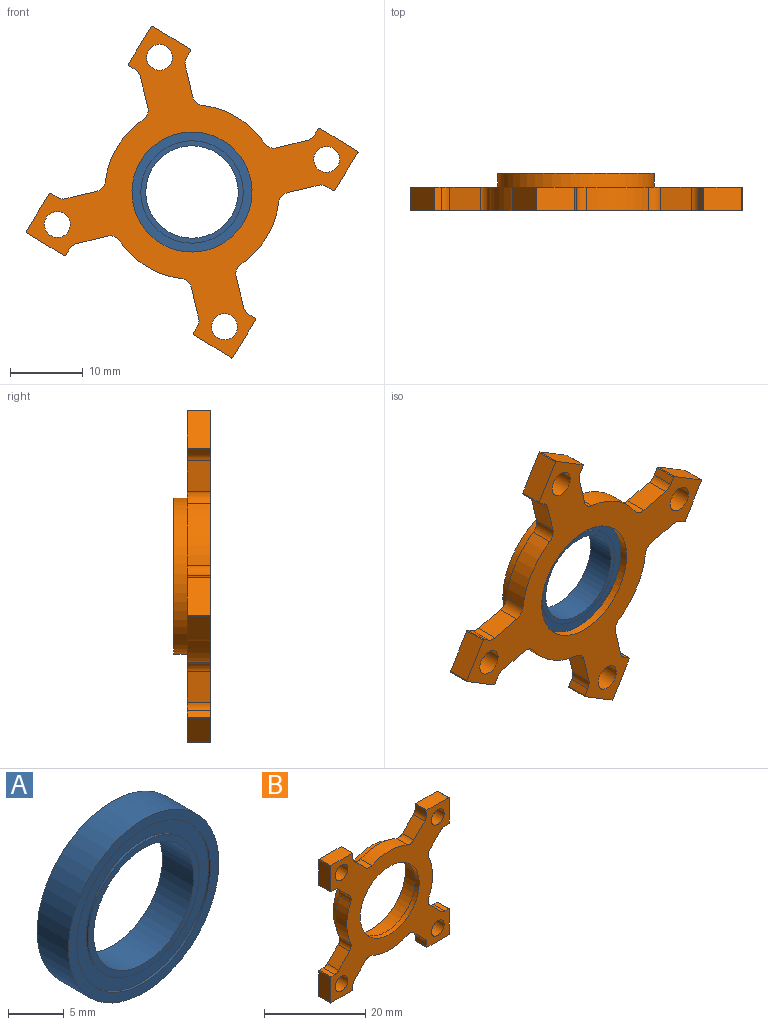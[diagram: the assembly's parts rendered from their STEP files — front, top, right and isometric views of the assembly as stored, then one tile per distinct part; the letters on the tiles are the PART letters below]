
ASSEMBLY  parts=2 mates=1
PART A: 12 faces, bbox 19.1x4x19.1 mm
  f0: cylinder r=7.04mm len=14.07mm, axis (0,-1,0), area 11.2mm2, adj f9,f11
  f1: cylinder r=8.48mm len=16.97mm, axis (0,-1,0), area 13.5mm2, adj f6,f11
  f2: cylinder r=7.04mm len=14.07mm, axis (0,1,0), area 11.2mm2, adj f7,f10
  f3: cylinder r=8.48mm len=16.97mm, axis (0,1,0), area 13.5mm2, adj f8,f10
  f4: cylinder r=6.35mm len=12.7mm, axis (0,-1,0), area 158.3mm2, adj f7,f9
  f5: cylinder r=9.53mm len=19.05mm, axis (0,-1,0), area 237.5mm2, adj f6,f8
  f6: plane 19.05x19.05mm, normal (0,-1,0), area 58.9mm2, adj f1,f5
  f7: plane 14.07x14.07mm, normal (0,1,0), area 28.8mm2, adj f2,f4
  f8: plane 19.05x19.05mm, normal (0,1,0), area 58.9mm2, adj f3,f5
  f9: plane 14.07x14.07mm, normal (0,-1,0), area 28.8mm2, adj f0,f4
  f10: plane 16.97x16.97mm, normal (0,1,0), area 70.6mm2, adj f2,f3
  f11: plane 16.97x16.97mm, normal (0,-1,0), area 70.6mm2, adj f0,f1
PART B: 67 faces, bbox 33.3x5.1x33.3 mm
  f0: cylinder r=8.26mm len=16.51mm, axis (0,1,0), area 58mm2, adj f38,f66
  f1: cylinder r=9.53mm len=19.05mm, axis (0,-1,0), area 237.1mm2, adj f65,f66
  f2: cylinder r=10.73mm len=21.46mm, axis (0,-1,0), area 128.5mm2, adj f10,f65
  f3: cylinder r=1.59mm len=3.18mm, axis (0,-1,0), area 6.1mm2, adj f10,f23,f24,f38
  f4: cylinder r=1.59mm len=3.18mm, axis (0,-1,0), area 6.1mm2, adj f10,f22,f23,f38
  f5: cylinder r=1.78mm len=3.56mm, axis (0,1,0), area 35.5mm2, adj f10,f38
  f6: cylinder r=1.78mm len=3.56mm, axis (0,1,0), area 35.5mm2, adj f10,f38
  f7: cylinder r=1.78mm len=3.56mm, axis (0,1,0), area 35.5mm2, adj f10,f38
  f8: cylinder r=1.78mm len=3.56mm, axis (0,1,0), area 35.5mm2, adj f10,f38
  f9: cylinder r=12mm len=9.95mm, axis (0,-1,0), area 32.6mm2, adj f10,f38,f61,f62
  f10: plane 33.27x33.27mm, normal (0,1,0), area 323.2mm2, adj f2,f3,f4,f5,f6,f7,f8,f9
  f11: plane 3.18x1.08mm, normal (1,0,0), area 3.4mm2, adj f10,f38,f48,f54
  f12: plane 6.1x3.18mm, normal (0,0,-1), area 19.4mm2, adj f10,f38,f48,f49
  f13: plane 6.1x3.18mm, normal (-1,0,0), area 19.4mm2, adj f10,f38,f49,f50
  f14: plane 3.18x1.08mm, normal (0,0,1), area 3.4mm2, adj f10,f38,f50,f53
  f15: plane 3.18x3.07mm, normal (-0.71,0,0.71), area 13.8mm2, adj f10,f38,f53,f63
  f16: cylinder r=12mm len=9.95mm, axis (0,-1,0), area 32.6mm2, adj f10,f38,f63,f64
  f17: plane 3.18x3.07mm, normal (-0.71,0,-0.71), area 13.8mm2, adj f10,f38,f52,f64
  f18: plane 3.18x1.08mm, normal (0,0,-1), area 3.4mm2, adj f10,f38,f39,f52
  f19: plane 6.1x3.18mm, normal (-1,0,0), area 19.4mm2, adj f10,f38,f39,f40
  f20: plane 6.1x3.18mm, normal (0,0,1), area 19.4mm2, adj f10,f38,f40,f43
  f21: plane 3.18x1.08mm, normal (1,0,0), area 3.4mm2, adj f10,f38,f43,f51
  f22: plane 3.18x3.07mm, normal (0.71,0,0.71), area 13.8mm2, adj f4,f10,f38,f51
  f23: cylinder r=12mm len=9.95mm, axis (0,-1,0), area 32.6mm2, adj f3,f4,f10,f38
  f24: plane 3.18x3.07mm, normal (-0.71,0,0.71), area 13.8mm2, adj f3,f10,f38,f58
  f25: plane 3.18x1.08mm, normal (-1,0,0), area 3.4mm2, adj f10,f38,f41,f58
  f26: plane 6.1x3.18mm, normal (0,0,1), area 19.4mm2, adj f10,f38,f41,f44
  f27: plane 6.1x3.18mm, normal (1,0,0), area 19.4mm2, adj f10,f38,f44,f45
  f28: plane 3.18x1.08mm, normal (0,0,-1), area 3.4mm2, adj f10,f38,f45,f57
  f29: plane 3.18x3.07mm, normal (0.71,0,-0.71), area 13.8mm2, adj f10,f38,f57,f59
  f30: cylinder r=12mm len=9.95mm, axis (0,-1,0), area 32.6mm2, adj f10,f38,f59,f60
  f31: plane 3.18x3.07mm, normal (0.71,0,0.71), area 13.8mm2, adj f10,f38,f56,f60
  f32: plane 3.18x1.08mm, normal (0,0,1), area 3.4mm2, adj f10,f38,f46,f56
  f33: plane 6.1x3.18mm, normal (1,0,0), area 19.4mm2, adj f10,f38,f46,f47
  f34: plane 6.1x3.18mm, normal (0,0,-1), area 19.4mm2, adj f10,f38,f42,f47
  f35: plane 3.18x1.08mm, normal (-1,0,0), area 3.4mm2, adj f10,f38,f42,f55
  f36: plane 3.18x3.07mm, normal (-0.71,0,-0.71), area 13.8mm2, adj f10,f38,f55,f62
  f37: plane 3.18x3.07mm, normal (0.71,0,-0.71), area 13.8mm2, adj f10,f38,f54,f61
  f38: plane 33.27x33.27mm, normal (0,-1,0), area 470.9mm2, adj f0,f3,f4,f5,f6,f7,f8,f9
  f39: cylinder r=0.13mm len=3.18mm, axis (0,-1,0), area 0.6mm2, adj f10,f18,f19,f38
  f40: cylinder r=0.13mm len=3.18mm, axis (0,1,0), area 0.6mm2, adj f10,f19,f20,f38
  f41: cylinder r=0.13mm len=3.18mm, axis (0,1,0), area 0.6mm2, adj f10,f25,f26,f38
  f42: cylinder r=0.13mm len=3.18mm, axis (0,1,0), area 0.6mm2, adj f10,f34,f35,f38
  f43: cylinder r=0.13mm len=3.18mm, axis (0,-1,0), area 0.6mm2, adj f10,f20,f21,f38
  f44: cylinder r=0.13mm len=3.18mm, axis (0,-1,0), area 0.6mm2, adj f10,f26,f27,f38
  f45: cylinder r=0.13mm len=3.18mm, axis (0,-1,0), area 0.6mm2, adj f10,f27,f28,f38
  f46: cylinder r=0.13mm len=3.18mm, axis (0,-1,0), area 0.6mm2, adj f10,f32,f33,f38
  f47: cylinder r=0.13mm len=3.18mm, axis (0,-1,0), area 0.6mm2, adj f10,f33,f34,f38
  f48: cylinder r=0.13mm len=3.18mm, axis (0,-1,0), area 0.6mm2, adj f10,f11,f12,f38
  f49: cylinder r=0.13mm len=3.18mm, axis (0,-1,0), area 0.6mm2, adj f10,f12,f13,f38
  f50: cylinder r=0.13mm len=3.18mm, axis (0,1,0), area 0.6mm2, adj f10,f13,f14,f38
  f51: cylinder r=1.59mm len=3.18mm, axis (0,-1,0), area 4mm2, adj f10,f21,f22,f38
  f52: cylinder r=1.59mm len=3.18mm, axis (0,-1,0), area 4mm2, adj f10,f17,f18,f38
  f53: cylinder r=1.59mm len=3.18mm, axis (0,-1,0), area 4mm2, adj f10,f14,f15,f38
  f54: cylinder r=1.59mm len=3.18mm, axis (0,-1,0), area 4mm2, adj f10,f11,f37,f38
  f55: cylinder r=1.59mm len=3.18mm, axis (0,-1,0), area 4mm2, adj f10,f35,f36,f38
  f56: cylinder r=1.59mm len=3.18mm, axis (0,-1,0), area 4mm2, adj f10,f31,f32,f38
  f57: cylinder r=1.59mm len=3.18mm, axis (0,-1,0), area 4mm2, adj f10,f28,f29,f38
  f58: cylinder r=1.59mm len=3.18mm, axis (0,-1,0), area 4mm2, adj f10,f24,f25,f38
  f59: cylinder r=1.59mm len=3.18mm, axis (0,-1,0), area 6.1mm2, adj f10,f29,f30,f38
  f60: cylinder r=1.59mm len=3.18mm, axis (0,-1,0), area 6.1mm2, adj f10,f30,f31,f38
  f61: cylinder r=1.59mm len=3.18mm, axis (0,-1,0), area 6.1mm2, adj f9,f10,f37,f38
  f62: cylinder r=1.59mm len=3.18mm, axis (0,-1,0), area 6.1mm2, adj f9,f10,f36,f38
  f63: cylinder r=1.59mm len=3.18mm, axis (0,-1,0), area 6.1mm2, adj f10,f15,f16,f38
  f64: cylinder r=1.59mm len=3.18mm, axis (0,-1,0), area 6.1mm2, adj f10,f16,f17,f38
  f65: plane 21.46x21.46mm, normal (0,1,0), area 76.8mm2, adj f1,f2
  f66: plane 19.05x19.05mm, normal (0,1,0), area 70.9mm2, adj f0,f1
PLACE A rot(axis=(0,1,0),31.4deg) t=(11.78,72.64,27.48)mm
PLACE B rot(axis=(0,1,0),31.4deg) t=(11.78,69.53,27.48)mm
MATE fastened B.f0 <-> A.f0  axis (0,1,0) through (11.78,70.65,27.48)mm
